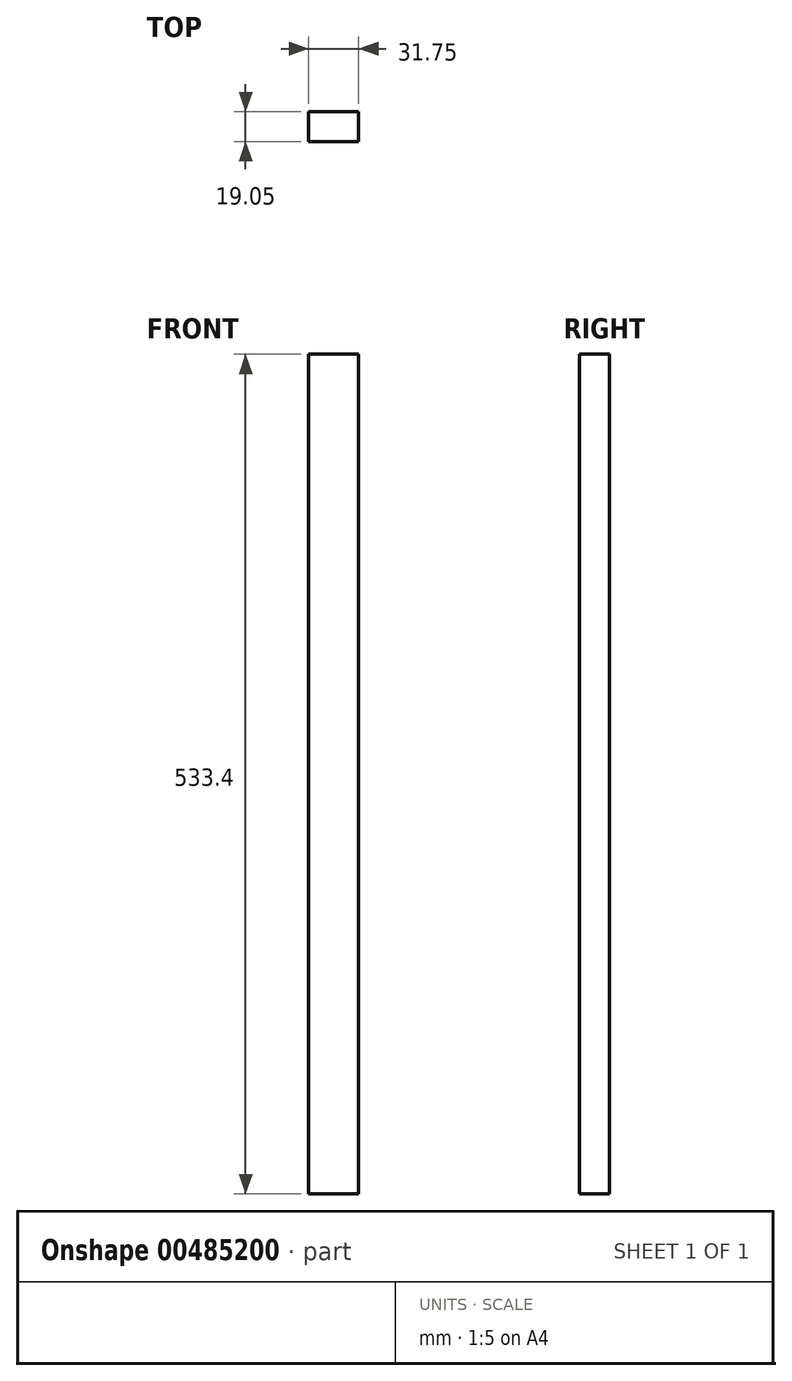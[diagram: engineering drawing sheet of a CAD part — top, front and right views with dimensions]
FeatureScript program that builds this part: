
annotation { "Feature Type Name" : "Feature", "Feature Type Description" : "" }
export const myFeature = defineFeature(function(context is Context, id is Id, definition is map)
    precondition{}
    {
        {
            var Q0;
            Q0=qCreatedBy(makeId("Front.planeOp"),FACE);
            var sketch = newSketch(context, id + "F0", { "sketchPlane" : qUnion([Q0])});
            skLineSegment(sketch, "E0.bottom", {"start": v(0, 0) * mm, "end": v(31.75, 0) * mm});
            skLineSegment(sketch, "E0.top", {"start": v(0, -533.4) * mm, "end": v(31.75, -533.4) * mm});
            skLineSegment(sketch, "E0.left", {"start": v(0, 0) * mm, "end": v(0, -533.4) * mm});
            skLineSegment(sketch, "E0.right", {"start": v(31.75, 0) * mm, "end": v(31.75, -533.4) * mm});
            skSolve(sketch);
        }
        {
            var Q0;
            Q0 = qSketchRegion(id + "F0", true);
            extrude(context, id + "F1", {"entities" : qUnion([Q0]), "oppositeDirection" : true, "depth" : 19.05 * mm});
        }
    });
